FCSTD DOCUMENT  (FreeCAD 0.16R)
Label: pi_zero_outline
License: All rights reserved
LicenseURL: http://en.wikipedia.org/wiki/All_rights_reserved
objects: Sketcher::SketchObject×1
note: 1 computed .brp shape members not serialized (recipe doc carries the construction recipe); baked Part::Feature solids carry a one-line shape summary decoded from their .brp

FEATURE [Sketcher::SketchObject] Sketch
  sketch-geometry (24):
    g0: LineSegment StartX=3 StartY=0 StartZ=0 EndX=62 EndY=0 EndZ=0
    g1: LineSegment StartX=65 StartY=3 StartZ=0 EndX=65 EndY=27.5 EndZ=0
    g2: LineSegment StartX=62 StartY=30.5 StartZ=0 EndX=3 EndY=30.5 EndZ=0
    g3: LineSegment StartX=0 StartY=27.5 StartZ=0 EndX=0 EndY=3 EndZ=0
    g4: ArcOfCircle CenterX=3 CenterY=27.5 CenterZ=0 NormalX=0 NormalY=0 NormalZ=1 Radius=3 StartAngle=1.5708 EndAngle=3.14159
    g5: ArcOfCircle CenterX=3 CenterY=3 CenterZ=0 NormalX=0 NormalY=0 NormalZ=1 Radius=3 StartAngle=3.14159 EndAngle=4.71239
    g6: ArcOfCircle CenterX=62 CenterY=3 CenterZ=0 NormalX=0 NormalY=0 NormalZ=1 Radius=3 StartAngle=4.71239 EndAngle=6.28319
    g7: ArcOfCircle CenterX=62 CenterY=27.5 CenterZ=0 NormalX=0 NormalY=0 NormalZ=1 Radius=3 StartAngle=0 EndAngle=1.5708
    g8: Circle CenterX=3.5 CenterY=26.5 CenterZ=0 NormalX=0 NormalY=0 NormalZ=1 Radius=1.375
    g9: Circle CenterX=61.5 CenterY=26.5 CenterZ=0 NormalX=0 NormalY=0 NormalZ=1 Radius=1.375
    g10: LineSegment [constr] StartX=3.5 StartY=26.5 StartZ=0 EndX=61.5 EndY=26.5 EndZ=0
    g11: Circle CenterX=3.5 CenterY=3.5 CenterZ=0 NormalX=0 NormalY=0 NormalZ=1 Radius=1.375
    g12: LineSegment [constr] StartX=3.5 StartY=26.5 StartZ=0 EndX=3.5 EndY=3.5 EndZ=0
    g13: Circle CenterX=61.5 CenterY=3.5 CenterZ=0 NormalX=0 NormalY=0 NormalZ=1 Radius=1.375
    g14: LineSegment [constr] StartX=3.5 StartY=3.5 StartZ=0 EndX=61.5 EndY=3.5 EndZ=0
    g15: LineSegment [constr] StartX=0 StartY=0 StartZ=0 EndX=122.024 EndY=0 EndZ=0
    g16: LineSegment [constr] StartX=0 StartY=0 StartZ=0 EndX=0 EndY=43.693 EndZ=0
    g17: LineSegment StartX=57.9 StartY=23.96 StartZ=0 EndX=57.9 EndY=29.04 EndZ=0
    g18: LineSegment StartX=57.9 StartY=29.04 StartZ=0 EndX=7.1 EndY=29.04 EndZ=0
    g19: LineSegment StartX=7.1 StartY=29.04 StartZ=0 EndX=7.1 EndY=23.96 EndZ=0
    g20: LineSegment StartX=7.1 StartY=23.96 StartZ=0 EndX=57.9 EndY=23.96 EndZ=0
    g21: Circle [constr] CenterX=32.5 CenterY=26.5 CenterZ=0 NormalX=0 NormalY=0 NormalZ=1 Radius=25.5267
    g22: LineSegment StartX=7.1 StartY=23.96 StartZ=0 EndX=57.9 EndY=29.04 EndZ=0
    g23: LineSegment StartX=57.9 StartY=23.96 StartZ=0 EndX=7.1 EndY=29.04 EndZ=0
  constraints (60):
    c: Horizontal(g0)
    c: Horizontal(g2)
    c: Vertical(g1)
    c: Vertical(g3)
    c: Tangent(g3,g4) = -1.5708
    c: Tangent(g2,g4) = -1.5708
    c: Tangent(g3,g5) = -1.5708
    c: Tangent(g0,g5) = -1.5708
    c: Tangent(g0,g6) = -1.5708
    c: Tangent(g1,g6) = -1.5708
    c: Tangent(g1,g7) = -1.5708
    c: Tangent(g2,g7) = -1.5708
    c: Radius(g4) = 3
    c: Equal(g4,g7)
    c: Equal(g7,g6)
    c: Equal(g6,g5)
    c: DistanceY(g0,g2) = 30.5
    c: DistanceX(g3,g1) = 65
    c: DistanceX(g3,g8) = 3.5
    c: Radius(g8) = 1.375
    c: Equal(g8,g9) = 1.375
    c: Coincident(g8,g10)
    c: Coincident(g9,g10)
    c: Distance(g10) = 58
    c: Angle(g10) = 0
    c: Equal(g8,g11) = 1.375
    c: Coincident(g8,g12)
    c: Coincident(g11,g12)
    c: Distance(g12) = 23
    c: Perpendicular(g12,g10)
    c: Equal(g8,g13) = 1.375
    c: Coincident(g11,g14)
    c: Coincident(g13,g14)
    c: Equal(g10,g14)
    c: Parallel(g14,g10)
    c: Coincident(g15,g-1)
    c: PointOnObject(g15,g-1)
    c: Coincident(g16,g-1)
    c: PointOnObject(g16,g-2)
    c: PointOnObject(g0,g15)
    c: PointOnObject(g3,g16)
    c: Coincident(g19,g20)
    c: Coincident(g20,g17)
    c: PointOnObject(g17,g21)
    c: PointOnObject(g19,g21)
    c: PointOnObject(g20,g21)
    c: Parallel(g20,g18)
    c: Coincident(g18,g19)
    c: PointOnObject(g18,g21)
    c: Coincident(g17,g18)
    c: Parallel(g17,g19)
    c: Parallel(g18,g2)
    c: DistanceX(g8,g21) = 29
    c: DistanceX(g18,g18) = 50.8
    c: DistanceY(g17,g17) = 5.08
    c: Coincident(g22,g19)
    c: Coincident(g22,g17)
    c: Coincident(g23,g17)
    c: Coincident(g23,g18)
    c: DistanceY(g0,g11) = 3.5
